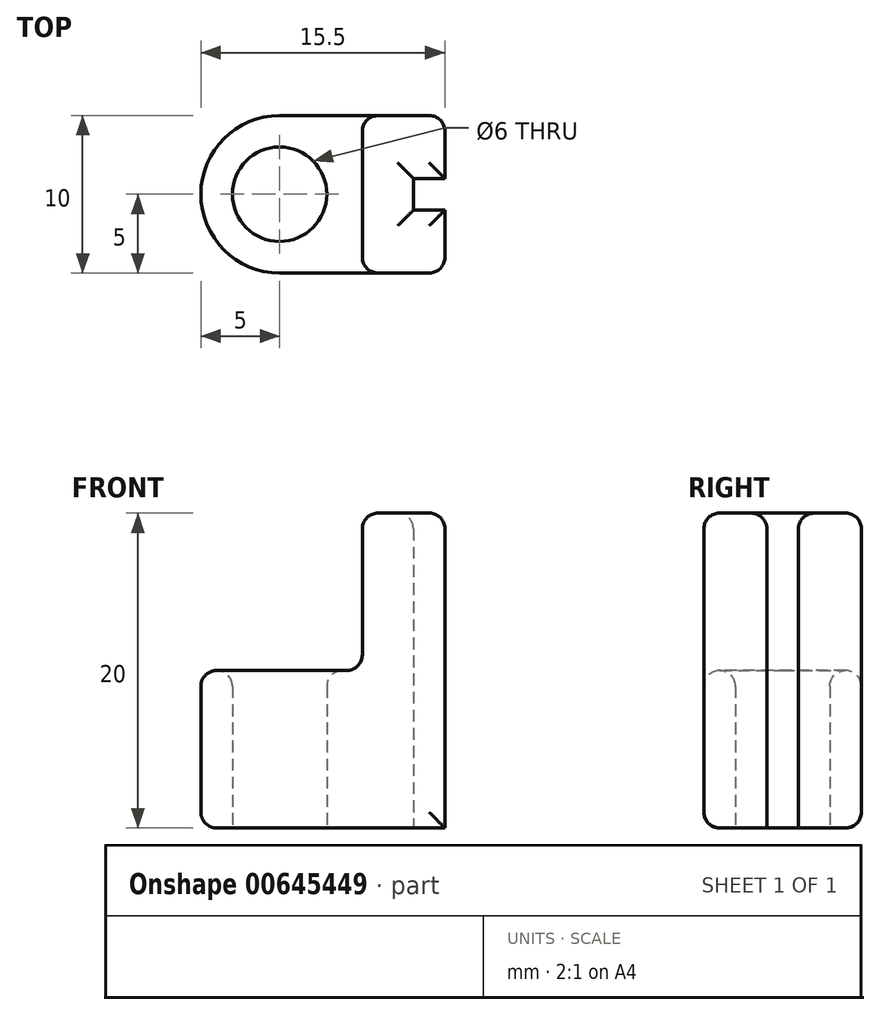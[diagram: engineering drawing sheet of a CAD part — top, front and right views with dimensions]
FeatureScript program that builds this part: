
annotation { "Feature Type Name" : "Feature", "Feature Type Description" : "" }
export const myFeature = defineFeature(function(context is Context, id is Id, definition is map)
    precondition{}
    {
        {
            var Q0;
            Q0=qCreatedBy(makeId("Top.planeOp"),FACE);
            var sketch = newSketch(context, id + "F0", { "sketchPlane" : qUnion([Q0])});
            skLineSegment(sketch, "E0.bottom", {"start": v(7.75, -5) * mm, "end": v(-2.75, -5) * mm});
            skLineSegment(sketch, "E0.top", {"start": v(7.75, 5) * mm, "end": v(-2.75, 5) * mm});
            skLineSegment(sketch, "E0.left", {"start": v(7.75, -5) * mm, "end": v(7.75, -1) * mm});
            skLineSegment(sketch, "E0.right", {"start": v(-7.75, 0) * mm, "end": v(-7.75, 0) * mm});
            skPoint(sketch, "E0.middle", {"position": v(0, 0) * mm});
            skLineSegment(sketch, "E1.bottom", {"start": v(7.75, 1) * mm, "end": v(5.75, 1) * mm});
            skLineSegment(sketch, "E1.top", {"start": v(7.75, -1) * mm, "end": v(5.75, -1) * mm});
            skLineSegment(sketch, "E1.right", {"start": v(5.75, 1) * mm, "end": v(5.75, -1) * mm});
            skCircle(sketch, "E2", {"center": v(-2.75, 0) * mm, "radius": 3 * mm});
            skPoint(sketch, "E3.visualSharp", {"position": v(-7.75, 5) * mm});
            skArc(sketch, "E3.filletArc", {"start": v(-2.75, 5) * mm, "mid": v(-6.29, 3.54) * mm, "end": v(-7.75, 0) * mm});
            skPoint(sketch, "E4.visualSharp", {"position": v(-7.75, -5) * mm});
            skArc(sketch, "E4.filletArc", {"start": v(-7.75, 0) * mm, "mid": v(-6.29, -3.54) * mm, "end": v(-2.75, -5) * mm});
            skLineSegment(sketch, "E5.trimOffspring", {"start": v(7.75, 1) * mm, "end": v(7.75, 5) * mm});
            skSolve(sketch);
        }
        {
            var Q0;
            Q0 = qSketchRegion(id + "F0", true);
            extrude(context, id + "F1", {"entities" : qUnion([Q0]), "depth" : 20 * mm, "offsetDistance" : 25 * mm});
        }
        {
            var Q0;
            Q0=makeQuery(id+"F1.opExtrude","CAP_FACE",FACE,{"disambiguationData":[OSD([sQuery(id+"F0.wireOp",EDGE,"E0.bottom"),sQuery(id+"F0.wireOp",EDGE,"E0.top"),sQuery(id+"F0.wireOp",EDGE,"E0.left"),sQuery(id+"F0.wireOp",EDGE,"E1.bottom"),sQuery(id+"F0.wireOp",EDGE,"E1.top"),sQuery(id+"F0.wireOp",EDGE,"E1.right"),sQuery(id+"F0.wireOp",EDGE,"E2"),sQuery(id+"F0.wireOp",EDGE,"E3.filletArc"),sQuery(id+"F0.wireOp",EDGE,"E4.filletArc"),sQuery(id+"F0.wireOp",EDGE,"E5.trimOffspring")])],"isStart":false});
            var sketch = newSketch(context, id + "F2", { "sketchPlane" : qUnion([Q0])});
            skPoint(sketch, "E6.oppositeSnap0", {"position": v(-7.75, 0) * mm});
            skLineSegment(sketch, "E6.bottom", {"start": v(2.5, 5) * mm, "end": v(-7.75, 5) * mm});
            skLineSegment(sketch, "E6.top", {"start": v(2.5, -5) * mm, "end": v(-7.75, -5) * mm});
            skLineSegment(sketch, "E6.left", {"start": v(2.5, 5) * mm, "end": v(2.5, -5) * mm});
            skLineSegment(sketch, "E6.right", {"start": v(-7.75, 5) * mm, "end": v(-7.75, -5) * mm});
            skSolve(sketch);
        }
        {
            var Q0;
            Q0 = qSketchRegion(id + "F2", true);
            extrude(context, id + "F3", {"entities" : qUnion([Q0]), "operationType" : NewBodyOperationType.REMOVE, "oppositeDirection" : true, "depth" : 10 * mm, "offsetDistance" : 25 * mm});
        }
        {
            var Q0;
            Q0=makeQuery(id+"F3.boolean.opBoolean","COPY",FACE,{"derivedFrom":makeQuery(id+"F3.opExtrude","CAP_FACE",FACE,{"disambiguationData":[OSD([sQuery(id+"F2.wireOp",EDGE,"E6.bottom"),sQuery(id+"F2.wireOp",EDGE,"E6.top"),sQuery(id+"F2.wireOp",EDGE,"E6.left"),sQuery(id+"F2.wireOp",EDGE,"E6.right")])],"isStart":false})});
            var Q1;
            Q1=makeQuery(id+"F1.opExtrude","CAP_FACE",FACE,{"disambiguationData":[OSD([sQuery(id+"F0.wireOp",EDGE,"E0.bottom"),sQuery(id+"F0.wireOp",EDGE,"E0.top"),sQuery(id+"F0.wireOp",EDGE,"E0.left"),sQuery(id+"F0.wireOp",EDGE,"E1.bottom"),sQuery(id+"F0.wireOp",EDGE,"E1.top"),sQuery(id+"F0.wireOp",EDGE,"E1.right"),sQuery(id+"F0.wireOp",EDGE,"E2"),sQuery(id+"F0.wireOp",EDGE,"E3.filletArc"),sQuery(id+"F0.wireOp",EDGE,"E4.filletArc"),sQuery(id+"F0.wireOp",EDGE,"E5.trimOffspring")])],"isStart":false});
            var Q2;
            Q2=makeQuery(id+"F1.opExtrude","SWEPT_FACE",FACE,{"disambiguationData":[OSD([sQuery(id+"F0.wireOp",EDGE,"E0.bottom")])]});
            var Q3;
            Q3=makeQuery(id+"F1.opExtrude","SWEPT_FACE",FACE,{"disambiguationData":[OSD([sQuery(id+"F0.wireOp",EDGE,"E0.top")])]});
            fillet(context, id + "F4", {"entities" : qUnion([Q0, Q1, Q2, Q3]), "radius" : 1 * mm, "tangentPropagation" : true, "allowEdgeOverflow" : false});
        }
    });
